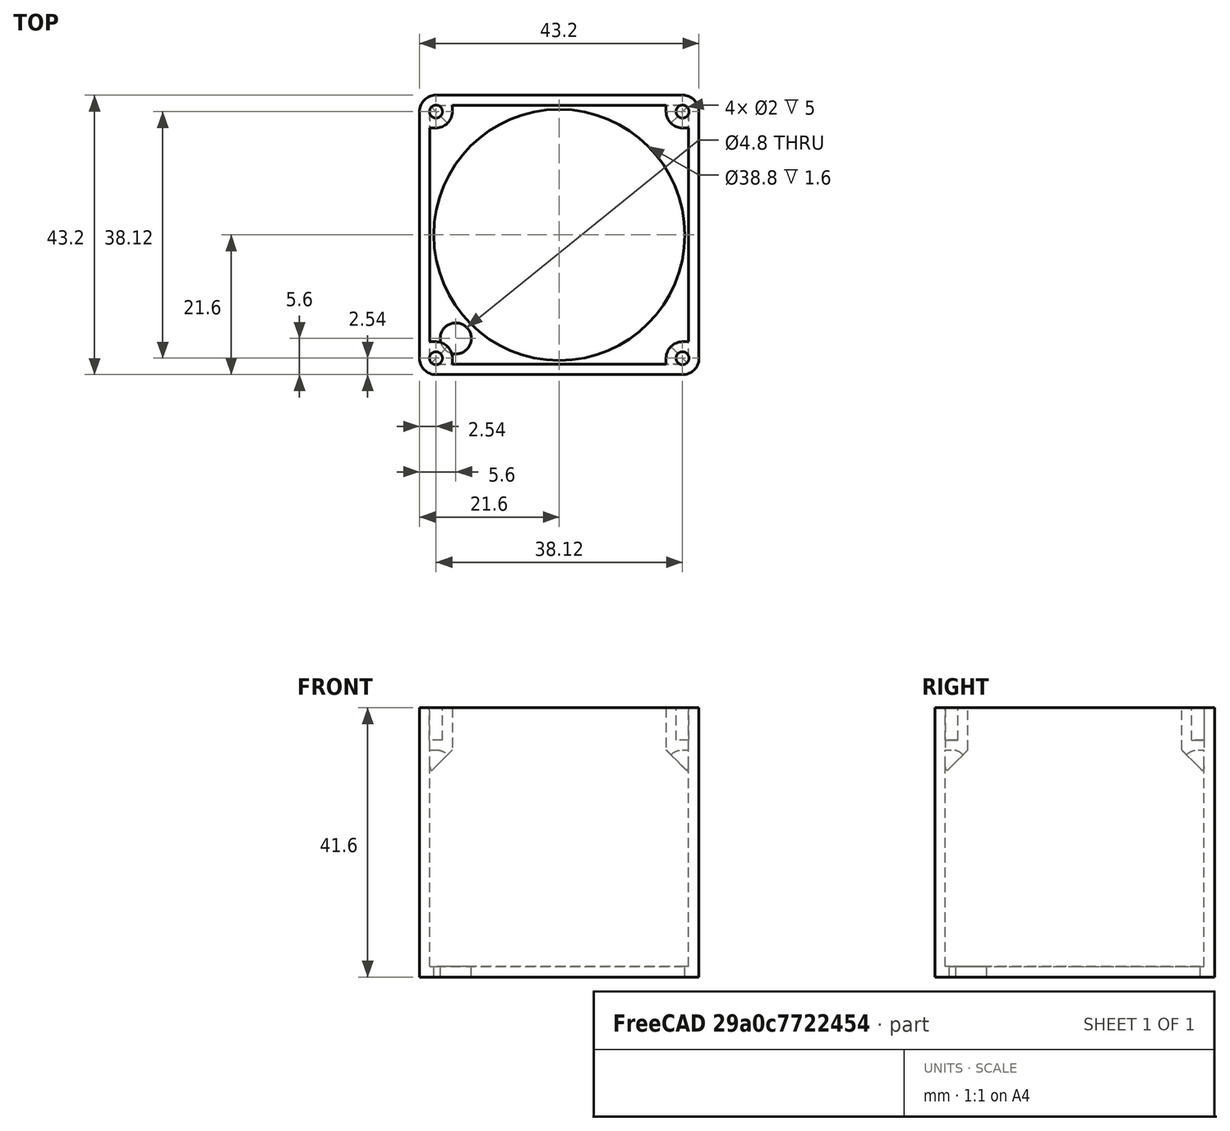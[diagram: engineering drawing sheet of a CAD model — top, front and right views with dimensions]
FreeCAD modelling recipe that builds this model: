
FCSTD DOCUMENT  (FreeCAD 0.16R)
Label: TinyPlayer_case
License: All rights reserved
LicenseURL: http://en.wikipedia.org/wiki/All_rights_reserved
objects: Part::Box×6, Part::Cylinder×6, Part::Fillet×6, Part::Cut×4, Part::Chamfer×4, Part::MultiFuse×3
note: 29 computed .brp shape members not serialized (recipe doc carries the construction recipe); baked Part::Feature solids carry a one-line shape summary decoded from their .brp

FEATURE [Part::Box] Box  label="Würfel"
  Height = 41.6
  Length = 43.2
  Width = 43.2
FEATURE [Part::Box] Box001  label="Würfel001"
  Height = 41.6
  Length = 40
  Placement = pos=(1.6,1.6,1.6) rot=(0,0,1;0rad)
  Width = 40
FEATURE [Part::Cut] Cut  label="Shell_raw"
  Base = -> Box
  Tool = -> Box001
FEATURE [Part::Cylinder] Cylinder  label="Speaker"
  Angle = 360
  Height = 1.6
  Placement = pos=(21.6,21.6,0) rot=(0,0,1;0rad)
  Radius = 19.4
FEATURE [Part::Cylinder] Cylinder001  label="IR"
  Angle = 360
  Height = 10
  Placement = pos=(5.6,5.6,0) rot=(0,0,1;0rad)
  Radius = 2.4
FEATURE [Part::Box] Box002  label="Würfel002"
  Height = 10
  Length = 5.08
  Placement = pos=(0,0,31.6) rot=(0,0,1;0rad)
  Width = 5.08
FEATURE [Part::Box] Box003  label="Würfel003"
  Height = 10
  Length = 5.08
  Placement = pos=(38.12,0,31.6) rot=(0,0,1;0rad)
  Width = 5.08
FEATURE [Part::Box] Box004  label="Würfel004"
  Height = 10
  Length = 5.08
  Placement = pos=(0,38.12,31.6) rot=(0,0,1;0rad)
  Width = 5.08
FEATURE [Part::Box] Box005  label="Würfel005"
  Height = 10
  Length = 5.08
  Placement = pos=(38.12,38.12,31.6) rot=(0,0,1;0rad)
  Width = 5.08
FEATURE [Part::Chamfer] Chamfer
  Base = -> Box004
  Edges = 2 edges r=3.5: [Edge8,Edge9]
FEATURE [Part::Chamfer] Chamfer001
  Base = -> Box005
  Edges = 2 edges r=3.5: [Edge4,Edge9]
FEATURE [Part::Chamfer] Chamfer002
  Base = -> Box003
  Edges = 2 edges r=3.5: [Edge4,Edge11]
FEATURE [Part::Chamfer] Chamfer003
  Base = -> Box002
  Edges = 2 edges r=3.5: [Edge8,Edge11]
FEATURE [Part::Fillet] Fillet
  Base = -> Cut
  Edges = 4 edges r=0.94: [Edge17,Edge18,Edge20,Edge22]
FEATURE [Part::Fillet] Fillet001
  Base = -> Chamfer003
  Edges = 1 edges r=2.54: [Edge6]
FEATURE [Part::Fillet] Fillet002
  Base = -> Chamfer
  Edges = 1 edges r=2.54: [Edge6]
FEATURE [Part::Fillet] Fillet003
  Base = -> Chamfer001
  Edges = 1 edges r=2.54: [Edge1]
FEATURE [Part::Fillet] Fillet004
  Base = -> Chamfer002
  Edges = 1 edges r=2.54: [Edge4]
FEATURE [Part::MultiFuse] Fusion  label="Holder"
  Shapes = -> [Fillet001,Fillet002,Fillet003,Fillet004]
FEATURE [Part::MultiFuse] Fusion001
  Shapes = -> [Fillet,Fusion]
FEATURE [Part::Fillet] Fillet005  label="Shell"
  Base = -> Fusion001
  Edges = 8 edges r=2.54: [Edge5,Edge13,Edge14,Edge22,Edge37,Edge43,Edge44,Edge50]
FEATURE [Part::Cylinder] Cylinder002  label="Zylinder"
  Angle = 360
  Height = 5
  Placement = pos=(2.54,2.54,36.6) rot=(0,0,1;0rad)
  Radius = 1
FEATURE [Part::Cylinder] Cylinder003  label="Zylinder001"
  Angle = 360
  Height = 5
  Placement = pos=(40.66,2.54,36.6) rot=(0,0,1;0rad)
  Radius = 1
FEATURE [Part::Cylinder] Cylinder004  label="Zylinder002"
  Angle = 360
  Height = 5
  Placement = pos=(2.54,40.66,36.6) rot=(0,0,1;0rad)
  Radius = 1
FEATURE [Part::Cylinder] Cylinder005  label="Zylinder003"
  Angle = 360
  Height = 5
  Placement = pos=(40.66,40.66,36.6) rot=(0,0,1;0rad)
  Radius = 1
FEATURE [Part::MultiFuse] Fusion002  label="Screws"
  Shapes = -> [Cylinder002,Cylinder004,Cylinder005,Cylinder003]
FEATURE [Part::Cut] Cut001
  Base = -> Fillet005
  Tool = -> Cylinder
FEATURE [Part::Cut] Cut002
  Base = -> Cut001
  Tool = -> Fusion002
FEATURE [Part::Cut] Cut003  label="Case"
  Base = -> Cut002
  Tool = -> Cylinder001
